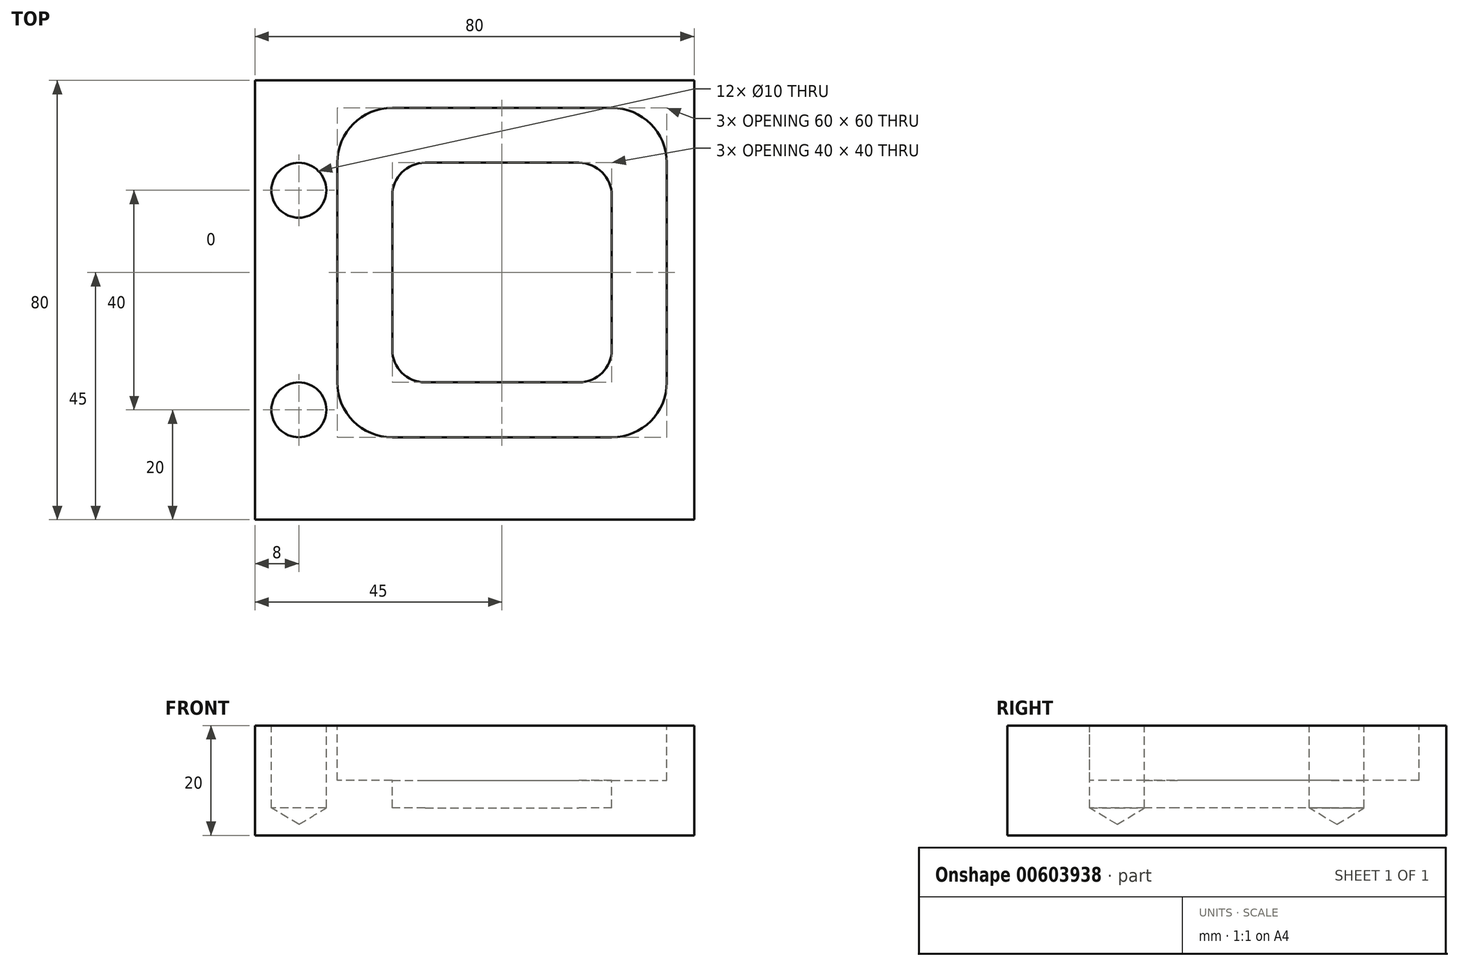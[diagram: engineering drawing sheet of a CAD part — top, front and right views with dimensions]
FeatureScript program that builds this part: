
annotation { "Feature Type Name" : "Feature", "Feature Type Description" : "" }
export const myFeature = defineFeature(function(context is Context, id is Id, definition is map)
    precondition{}
    {
        {
            var Q0;
            Q0=qCreatedBy(makeId("Top.planeOp"),FACE);
            var sketch = newSketch(context, id + "F0", { "sketchPlane" : qUnion([Q0])});
            skLineSegment(sketch, "E0.bottom", {"start": v(-40, 40) * mm, "end": v(40, 40) * mm});
            skLineSegment(sketch, "E0.top", {"start": v(-40, -40) * mm, "end": v(40, -40) * mm});
            skLineSegment(sketch, "E0.left", {"start": v(-40, 40) * mm, "end": v(-40, -40) * mm});
            skLineSegment(sketch, "E0.right", {"start": v(40, 40) * mm, "end": v(40, -40) * mm});
            skPoint(sketch, "E0.middle", {"position": v(0, 0) * mm});
            skSolve(sketch);
        }
        {
            var Q0;
            Q0=makeQuery(id+"F0.imprint","IMPRINT",FACE,{"disambiguationData":[TD([[makeQuery(id+"F0.imprint","IMPRINT",EDGE,{"derivedFrom":sQuery(id+"F0.wireOp",EDGE,"E0.bottom")}),-1.0]])]});
            extrude(context, id + "F1", {"entities" : qUnion([Q0]), "depth" : 20 * mm, "offsetDistance" : 25 * mm});
        }
        {
            var Q0;
            Q0=makeQuery(id+"F1.opExtrude","CAP_FACE",FACE,{"disambiguationData":[OSD([sQuery(id+"F0.wireOp",EDGE,"E0.bottom"),sQuery(id+"F0.wireOp",EDGE,"E0.top"),sQuery(id+"F0.wireOp",EDGE,"E0.left"),sQuery(id+"F0.wireOp",EDGE,"E0.right")])],"isStart":false});
            var sketch = newSketch(context, id + "F2", { "sketchPlane" : qUnion([Q0])});
            skCircle(sketch, "E1", {"center": v(-32, 20) * mm, "radius": 4 * mm});
            skCircle(sketch, "E2", {"center": v(-32, -20) * mm, "radius": 4 * mm});
            skSolve(sketch);
        }
        {
            var Q0;
            Q0=sQuery(id+"F2.wireOp",VERTEX,"E1.center");
            var Q1;
            Q1=sQuery(id+"F2.wireOp",VERTEX,"E2.center");
            var Q2;
            Q2=makeQuery(id+"F1.opExtrude","SWEPT_BODY",BODY,{"disambiguationData":[OSD([sQuery(id+"F0.wireOp",EDGE,"E0.bottom"),sQuery(id+"F0.wireOp",EDGE,"E0.top"),sQuery(id+"F0.wireOp",EDGE,"E0.left"),sQuery(id+"F0.wireOp",EDGE,"E0.right")])]});
            hole(context, id + "F3", {"style" : HoleStyle.SIMPLE, "endStyle" : HoleEndStyle.BLIND, "holeDiameter" : 10 * mm, "majorDiameter" : 5 * mm, "holeDepth" : 15 * mm, "isTappedThrough" : true, "tappedDepth" : 12 * mm, "tapClearance" : 3, "locations" : qUnion([Q0, Q1]), "scope" : qUnion([Q2])});
        }
        {
            var Q0;
            Q0=makeQuery(id+"F1.opExtrude","CAP_FACE",FACE,{"disambiguationData":[OSD([sQuery(id+"F0.wireOp",EDGE,"E0.bottom"),sQuery(id+"F0.wireOp",EDGE,"E0.top"),sQuery(id+"F0.wireOp",EDGE,"E0.left"),sQuery(id+"F0.wireOp",EDGE,"E0.right")])],"isStart":false});
            var sketch = newSketch(context, id + "F4", { "sketchPlane" : qUnion([Q0])});
            skLineSegment(sketch, "E3.bottom", {"start": v(-15, 35) * mm, "end": v(25, 35) * mm});
            skLineSegment(sketch, "E3.top", {"start": v(-15, -25) * mm, "end": v(25, -25) * mm});
            skLineSegment(sketch, "E3.left", {"start": v(-25, 25) * mm, "end": v(-25, -15) * mm});
            skLineSegment(sketch, "E3.right", {"start": v(35, 25) * mm, "end": v(35, -15) * mm});
            skPoint(sketch, "E4.visualSharp", {"position": v(35, 35) * mm});
            skArc(sketch, "E4.filletArc", {"start": v(35, 25) * mm, "mid": v(32.07, 32.07) * mm, "end": v(25, 35) * mm});
            skPoint(sketch, "E5.visualSharp", {"position": v(-25, 35) * mm});
            skArc(sketch, "E5.filletArc", {"start": v(-15, 35) * mm, "mid": v(-22.07, 32.07) * mm, "end": v(-25, 25) * mm});
            skPoint(sketch, "E6.visualSharp", {"position": v(-25, -25) * mm});
            skArc(sketch, "E6.filletArc", {"start": v(-25, -15) * mm, "mid": v(-22.07, -22.07) * mm, "end": v(-15, -25) * mm});
            skPoint(sketch, "E7.visualSharp", {"position": v(35, -25) * mm});
            skArc(sketch, "E7.filletArc", {"start": v(25, -25) * mm, "mid": v(32.07, -22.07) * mm, "end": v(35, -15) * mm});
            skLineSegment(sketch, "E8.bottom", {"start": v(-9, 25) * mm, "end": v(19, 25) * mm});
            skLineSegment(sketch, "E8.top", {"start": v(-9, -15) * mm, "end": v(19, -15) * mm});
            skLineSegment(sketch, "E8.left", {"start": v(-15, 19) * mm, "end": v(-15, -9) * mm});
            skLineSegment(sketch, "E8.right", {"start": v(25, 19) * mm, "end": v(25, -9) * mm});
            skArc(sketch, "E9.filletArc", {"start": v(-9, 25) * mm, "mid": v(-13.24, 23.24) * mm, "end": v(-15, 19) * mm});
            skArc(sketch, "E10.filletArc", {"start": v(25, 19) * mm, "mid": v(23.24, 23.24) * mm, "end": v(19, 25) * mm});
            skArc(sketch, "E11.filletArc", {"start": v(19, -15) * mm, "mid": v(23.24, -13.24) * mm, "end": v(25, -9) * mm});
            skArc(sketch, "E12.filletArc", {"start": v(-15, -9) * mm, "mid": v(-13.24, -13.24) * mm, "end": v(-9, -15) * mm});
            skSolve(sketch);
        }
        {
            var Q0;
            Q0=makeQuery(id+"F4.imprint","IMPRINT",FACE,{"disambiguationData":[TD([[makeQuery(id+"F4.imprint","IMPRINT",EDGE,{"derivedFrom":sQuery(id+"F4.wireOp",EDGE,"E3.bottom")}),-1.0]])]});
            extrude(context, id + "F5", {"entities" : qUnion([Q0]), "operationType" : NewBodyOperationType.REMOVE, "oppositeDirection" : true, "depth" : 10 * mm, "offsetDistance" : 25 * mm});
        }
        {
            var Q0;
            Q0=makeQuery(id+"F5.boolean.opBoolean","SPLIT",FACE,{"disambiguationData":[TD([makeQuery(id+"F5.opExtrude","SWEPT_FACE",FACE,{"disambiguationData":[OSD([sQuery(id+"F4.wireOp",EDGE,"E8.bottom")])]})])],"derivedFrom":makeQuery(id+"F1.opExtrude","CAP_FACE",FACE,{"disambiguationData":[OSD([sQuery(id+"F0.wireOp",EDGE,"E0.bottom"),sQuery(id+"F0.wireOp",EDGE,"E0.top"),sQuery(id+"F0.wireOp",EDGE,"E0.left"),sQuery(id+"F0.wireOp",EDGE,"E0.right")])],"isStart":false})});
            extrude(context, id + "F6", {"entities" : qUnion([Q0]), "operationType" : NewBodyOperationType.REMOVE, "oppositeDirection" : true, "depth" : 15 * mm, "offsetDistance" : 25 * mm});
        }
    });
